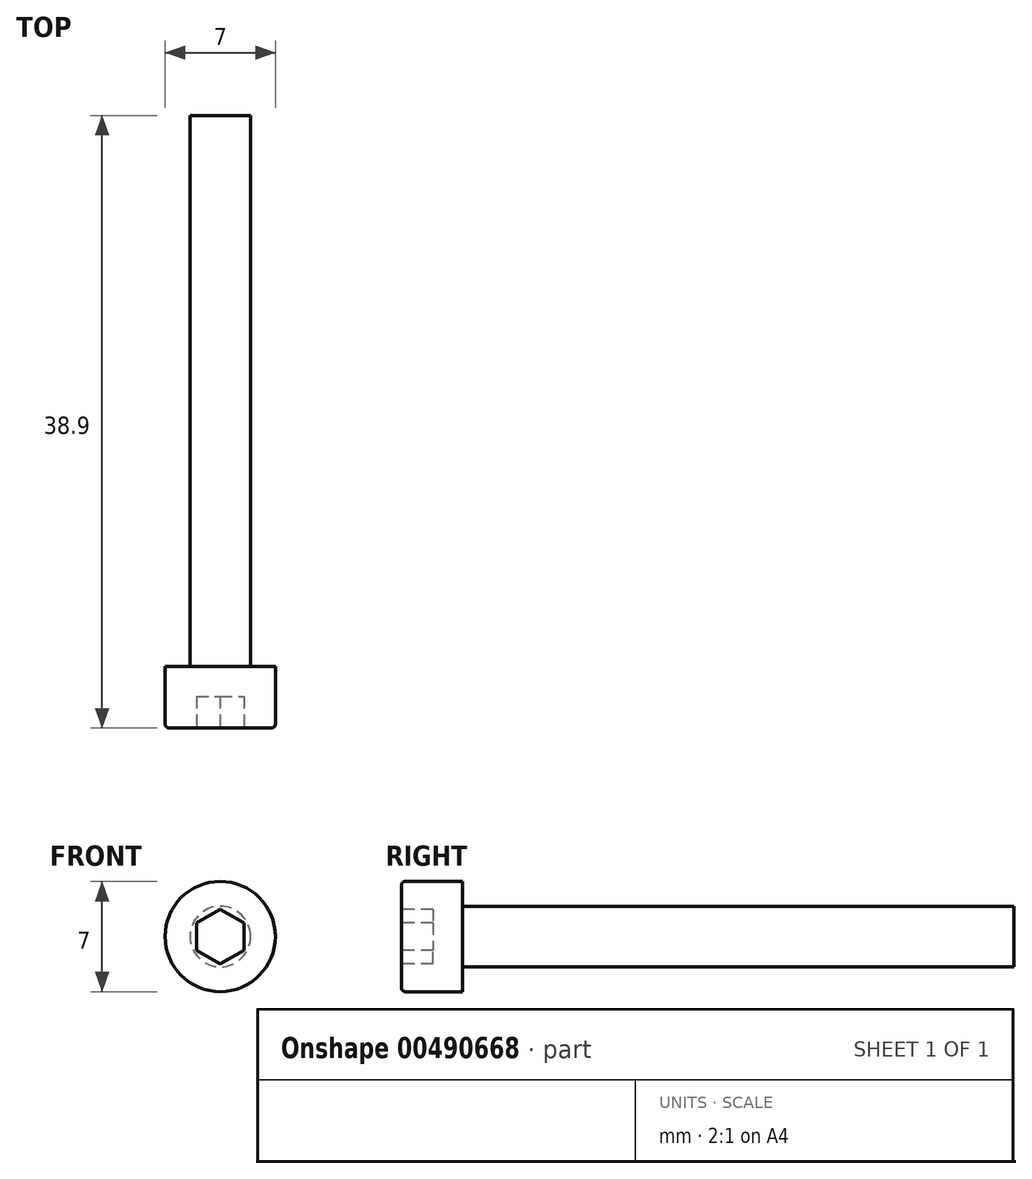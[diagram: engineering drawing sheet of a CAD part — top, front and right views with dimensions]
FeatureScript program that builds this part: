
annotation { "Feature Type Name" : "Feature", "Feature Type Description" : "" }
export const myFeature = defineFeature(function(context is Context, id is Id, definition is map)
    precondition{}
    {
        {
            var Q0;
            Q0=qCreatedBy(makeId("Front.planeOp"),FACE);
            var sketch = newSketch(context, id + "F0", { "sketchPlane" : qUnion([Q0])});
            skCircle(sketch, "E0", {"center": v(0, 0) * mm, "radius": 3.5 * mm});
            skCircle(sketch, "E1", {"center": v(0, 0) * mm, "radius": 1.93 * mm});
            skSolve(sketch);
        }
        {
            var Q0;
            Q0=makeQuery(id+"F0.imprint","IMPRINT",FACE,{"disambiguationData":[TD([[makeQuery(id+"F0.imprint","IMPRINT",EDGE,{"derivedFrom":sQuery(id+"F0.wireOp",EDGE,"E1")}),1.0]])]});
            var Q1;
            Q1=makeQuery(id+"F0.imprint","IMPRINT",FACE,{"disambiguationData":[TD([[makeQuery(id+"F0.imprint","IMPRINT",EDGE,{"derivedFrom":sQuery(id+"F0.wireOp",EDGE,"E0")}),1.0]])]});
            extrude(context, id + "F1", {"entities" : qUnion([Q0, Q1]), "depth" : 3.9 * mm});
        }
        {
            var Q0;
            Q0=makeQuery(id+"F0.imprint","IMPRINT",FACE,{"disambiguationData":[TD([[makeQuery(id+"F0.imprint","IMPRINT",EDGE,{"derivedFrom":sQuery(id+"F0.wireOp",EDGE,"E1")}),1.0]])]});
            extrude(context, id + "F2", {"entities" : qUnion([Q0]), "operationType" : NewBodyOperationType.ADD, "oppositeDirection" : true, "depth" : 35 * mm, "offsetDistance" : 25 * mm});
        }
        {
            var Q0;
            Q0=makeQuery(id+"F1.opExtrude","CAP_FACE",FACE,{"disambiguationData":[OSD([sQuery(id+"F0.wireOp",EDGE,"E0")])],"isStart":false});
            var sketch = newSketch(context, id + "F3", { "sketchPlane" : qUnion([Q0])});
            skCircle(sketch, "E2.cCircle", {"center": v(0, 0) * mm, "radius": 1.5 * mm, "construction": true});
            skLineSegment(sketch, "E2.0", {"start": v(1.5, 0.87) * mm, "end": v(1.5, -0.87) * mm});
            skLineSegment(sketch, "E2.1", {"start": v(1.5, -0.87) * mm, "end": v(0, -1.73) * mm});
            skLineSegment(sketch, "E2.2", {"start": v(0, -1.73) * mm, "end": v(-1.5, -0.87) * mm});
            skLineSegment(sketch, "E2.3", {"start": v(-1.5, -0.87) * mm, "end": v(-1.5, 0.87) * mm});
            skLineSegment(sketch, "E2.4", {"start": v(-1.5, 0.87) * mm, "end": v(0, 1.73) * mm});
            skLineSegment(sketch, "E2.5", {"start": v(0, 1.73) * mm, "end": v(1.5, 0.87) * mm});
            skPoint(sketch, "E2.0.midPoint", {"position": v(1.5, 0) * mm});
            skSolve(sketch);
        }
        {
            var Q0;
            Q0=makeQuery(id+"F3.imprint","IMPRINT",FACE,{"disambiguationData":[TD([[makeQuery(id+"F3.imprint","IMPRINT",EDGE,{"derivedFrom":sQuery(id+"F3.wireOp",EDGE,"E2.0")}),-1.0]])]});
            extrude(context, id + "F4", {"entities" : qUnion([Q0]), "operationType" : NewBodyOperationType.REMOVE, "oppositeDirection" : true, "depth" : 2 * mm});
        }
        {
            var Q0;
            Q0=makeQuery(id+"F1.opExtrude","CAP_EDGE",EDGE,{"disambiguationData":[OSD([sQuery(id+"F0.wireOp",EDGE,"E0")])],"isStart":false});
            fillet(context, id + "F5", {"entities" : qUnion([Q0]), "radius" : .25 * mm, "tangentPropagation" : true, "allowEdgeOverflow" : false});
        }
    });
